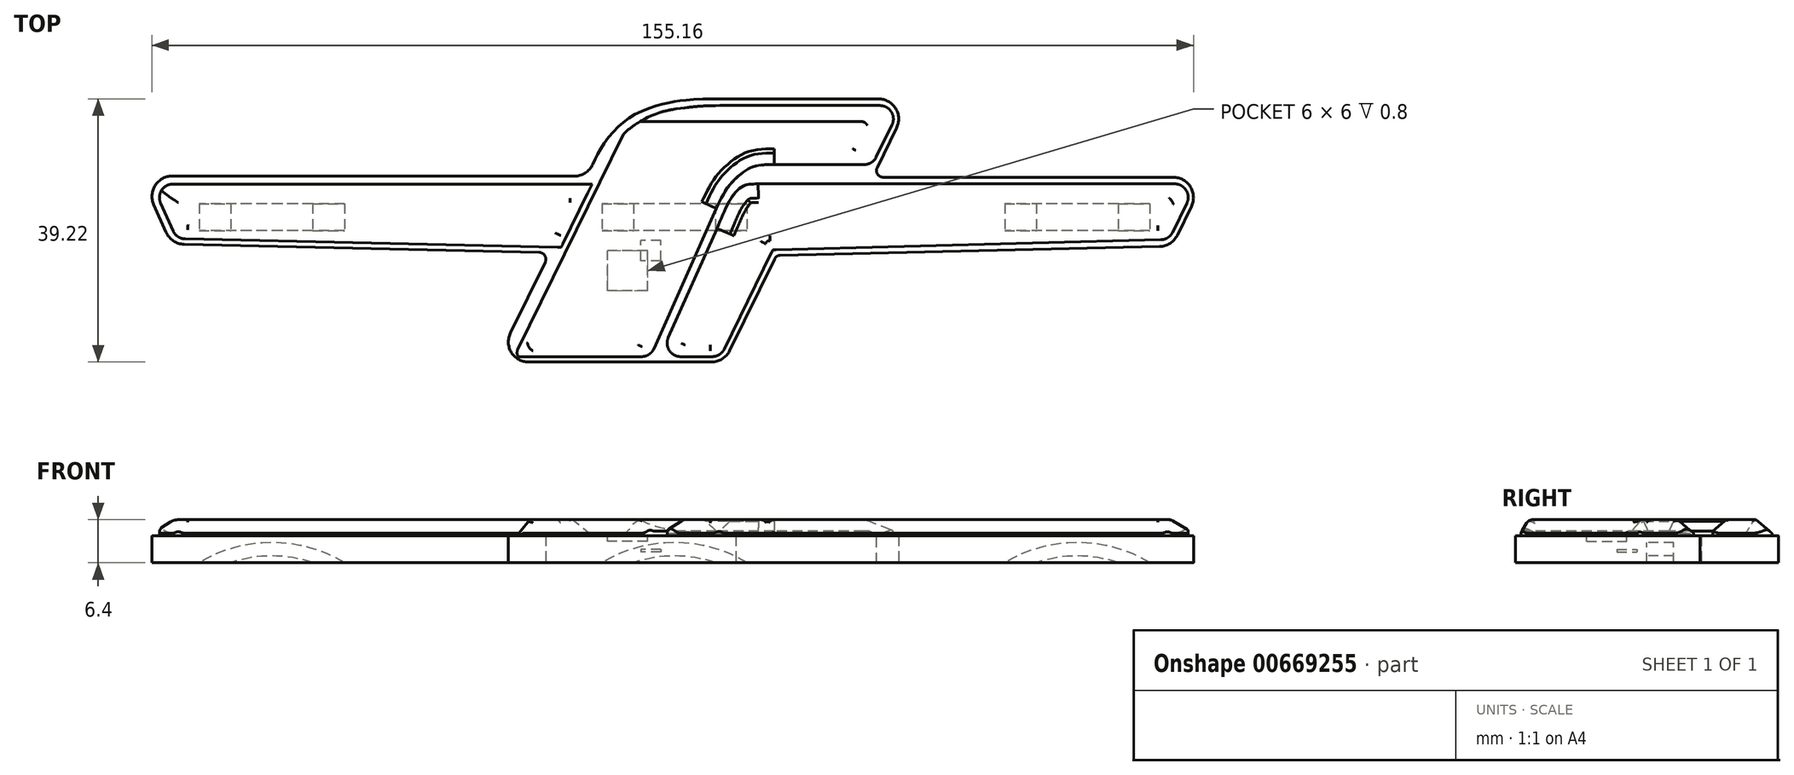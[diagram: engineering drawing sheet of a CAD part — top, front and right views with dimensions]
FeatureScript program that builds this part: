
annotation { "Feature Type Name" : "Feature", "Feature Type Description" : "" }
export const myFeature = defineFeature(function(context is Context, id is Id, definition is map)
    precondition{}
    {
        {
            var Q0;
            Q0=qCreatedBy(makeId("Top.planeOp"),FACE);
            var sketch = newSketch(context, id + "F0", { "sketchPlane" : qUnion([Q0])});
            skLineSegment(sketch, "E0", {"start": v(-9.3, -1.65) * mm, "end": v(-13.28, -9.8) * mm});
            skLineSegment(sketch, "E1", {"start": v(-13.28, -9.8) * mm, "end": v(3.7, -9.8) * mm});
            skLineSegment(sketch, "E2", {"start": v(3.7, -9.8) * mm, "end": v(7.58, -1.85) * mm});
            skLineSegment(sketch, "E3", {"start": v(-9.3, -1.65) * mm, "end": v(-37.48, -1) * mm});
            skLineSegment(sketch, "E4", {"start": v(-37.48, -1) * mm, "end": v(-39.73, 4.05) * mm});
            skLineSegment(sketch, "E5", {"start": v(-6.5, 4.05) * mm, "end": v(-39.73, 4.05) * mm});
            skLineSegment(sketch, "E6", {"start": v(7.58, -1.85) * mm, "end": v(37.05, -1.17) * mm});
            skLineSegment(sketch, "E7", {"start": v(37.05, -1.17) * mm, "end": v(39.56, 3.96) * mm});
            skLineSegment(sketch, "E8", {"start": v(39.56, 3.96) * mm, "end": v(14.75, 3.96) * mm});
            skLineSegment(sketch, "E9", {"start": v(14.75, 3.96) * mm, "end": v(17.6, 9.8) * mm});
            skLineSegment(sketch, "E10", {"start": v(17.6, 9.8) * mm, "end": v(4.58, 9.8) * mm});
            skLineSegment(sketch, "E11", {"start": v(-4.8, -9.8) * mm, "end": v(4.8, 9.8) * mm, "construction": true});
            skLineSegment(sketch, "E12", {"start": v(-9.3, -1.65) * mm, "end": v(-6.5, 4.05) * mm});
            skFitSpline(sketch, "E13", {"points": [v(-6.5, 4.05) * mm, v(-5.96, 5.22) * mm, v(-5.41, 6.24) * mm, v(-4.34, 7.56) * mm, v(-3.15, 8.53) * mm, v(-1.39, 9.28) * mm, v(-0.1, 9.58) * mm, v(1.1, 9.73) * mm, v(4.58, 9.8) * mm], "startDerivative": vector(5.08, 10.85) * mm, "endDerivative": vector(21.51, -0.42) * mm});
            skSolve(sketch);
        }
        {
            var Q0;
            Q0 = qSketchRegion(id + "F0", true);
            extrude(context, id + "F1", {"entities" : qUnion([Q0]), "depth" : 2 * mm, "offsetDistance" : 25 * mm});
        }
        {
            var Q0;
            Q0=makeQuery(id+"F1.opExtrude","CAP_FACE",FACE,{"disambiguationData":[OSD([sQuery(id+"F0.wireOp",EDGE,"E0"),sQuery(id+"F0.wireOp",EDGE,"E1"),sQuery(id+"F0.wireOp",EDGE,"E2"),sQuery(id+"F0.wireOp",EDGE,"E3"),sQuery(id+"F0.wireOp",EDGE,"E4"),sQuery(id+"F0.wireOp",EDGE,"E5"),sQuery(id+"F0.wireOp",EDGE,"E6"),sQuery(id+"F0.wireOp",EDGE,"E7"),sQuery(id+"F0.wireOp",EDGE,"E8"),sQuery(id+"F0.wireOp",EDGE,"E9"),sQuery(id+"F0.wireOp",EDGE,"E10"),sQuery(id+"F0.wireOp",EDGE,"b49870b3-532a-455c-8938-6e246f278ffe")])],"isStart":false});
            var sketch = newSketch(context, id + "F2", { "sketchPlane" : qUnion([Q0])});
            skLineSegment(sketch, "E14.0", {"start": v(-12.42, -9.4) * mm, "end": v(-1.8, -9.4) * mm});
            skLineSegment(sketch, "E14.2", {"start": v(-5.32, 5.12) * mm, "end": v(-12.42, -9.4) * mm});
            skLineSegment(sketch, "E14.4", {"start": v(-37.1, -0.61) * mm, "end": v(-8.44, -1.26) * mm});
            skLineSegment(sketch, "E14.7", {"start": v(-6.14, 3.45) * mm, "end": v(-38.9, 3.45) * mm});
            skLineSegment(sketch, "E14.9", {"start": v(-38.9, 3.45) * mm, "end": v(-37.1, -0.61) * mm});
            skLineSegment(sketch, "E14.14", {"start": v(7.32, -1.46) * mm, "end": v(36.84, -0.67) * mm});
            skLineSegment(sketch, "E14.16", {"start": v(36.84, -0.67) * mm, "end": v(38.87, 3.47) * mm});
            skLineSegment(sketch, "E14.18", {"start": v(38.87, 3.47) * mm, "end": v(6.25, 3.47) * mm});
            skLineSegment(sketch, "E14.20", {"start": v(14.76, 4.91) * mm, "end": v(16.9, 9.3) * mm});
            skLineSegment(sketch, "E14.22", {"start": v(16.9, 9.3) * mm, "end": v(4.7, 9.3) * mm});
            skLineSegment(sketch, "E15", {"start": v(3.12, 1.64) * mm, "end": v(-1.8, -9.4) * mm});
            skLineSegment(sketch, "E16", {"start": v(14.76, 4.91) * mm, "end": v(7.44, 4.91) * mm});
            skLineSegment(sketch, "E17", {"start": v(-5.85, 4.04) * mm, "end": v(-5.32, 5.12) * mm});
            skFitSpline(sketch, "E18", {"points": [v(-5.85, 4.04) * mm, v(-4.97, 5.75) * mm, v(-3.99, 7.02) * mm, v(-2.6, 8.1) * mm, v(-0.84, 8.86) * mm, v(0.9, 9.16) * mm, v(2.28, 9.28) * mm, v(4.7, 9.3) * mm], "startDerivative": vector(5.74, 12.1) * mm, "endDerivative": vector(15.8, -0.05) * mm});
            skFitSpline(sketch, "E19", {"points": [v(3.12, 1.64) * mm, v(3.63, 2.68) * mm, v(4.24, 3.55) * mm, v(4.98, 4.23) * mm, v(5.54, 4.61) * mm, v(6.09, 4.81) * mm, v(6.58, 4.89) * mm, v(7.44, 4.91) * mm], "startDerivative": vector(2.92, 6.26) * mm, "endDerivative": vector(6.3, 0.08) * mm});
            skLineSegment(sketch, "E20", {"start": v(-1.1, -9.4) * mm, "end": v(3.16, 0.16) * mm});
            skFitSpline(sketch, "E21", {"points": [v(3.16, 0.16) * mm, v(3.58, 1.14) * mm, v(4, 2.02) * mm, v(4.38, 2.63) * mm, v(4.79, 3.1) * mm, v(5.17, 3.33) * mm, v(5.46, 3.42) * mm, v(5.77, 3.46) * mm, v(6.25, 3.47) * mm], "startDerivative": vector(2.45, 5.8) * mm, "endDerivative": vector(4.54, 0.1) * mm});
            skLineSegment(sketch, "E22.trimOffspring", {"start": v(-1.1, -9.4) * mm, "end": v(3.43, -9.4) * mm});
            skLineSegment(sketch, "E23", {"start": v(3.43, -9.4) * mm, "end": v(7.32, -1.46) * mm});
            skSolve(sketch);
        }
        {
            var Q0;
            Q0=makeQuery(id+"F2.imprint","IMPRINT",FACE,{"disambiguationData":[TD([[makeQuery(id+"F2.imprint","IMPRINT",EDGE,{"derivedFrom":sQuery(id+"F2.wireOp",EDGE,"E14.0")}),-1.0]])]});
            var sketch = newSketch(context, id + "F3", { "sketchPlane" : qUnion([Q0])});
            skLineSegment(sketch, "E24.bottom", {"start": v(-2, -4.5) * mm, "end": v(-5, -4.5) * mm});
            skLineSegment(sketch, "E24.top", {"start": v(-2, -1.5) * mm, "end": v(-5, -1.5) * mm});
            skLineSegment(sketch, "E24.left", {"start": v(-2, -4.5) * mm, "end": v(-2, -1.5) * mm});
            skLineSegment(sketch, "E24.right", {"start": v(-5, -4.5) * mm, "end": v(-5, -1.5) * mm});
            skPoint(sketch, "E24.middle", {"position": v(-3.5, -3) * mm});
            skSolve(sketch);
        }
        {
            var Q0;
            Q0=makeQuery(id+"F3.imprint","IMPRINT",FACE,{"disambiguationData":[TD([[makeQuery(id+"F3.imprint","IMPRINT",EDGE,{"derivedFrom":sQuery(id+"F3.wireOp",EDGE,"E24.bottom")}),-1.0]])]});
            extrude(context, id + "F4", {"entities" : qUnion([Q0]), "operationType" : NewBodyOperationType.REMOVE, "oppositeDirection" : true, "depth" : .4 * mm, "offsetDistance" : 25 * mm});
        }
        {
            var Q0;
            Q0=makeQuery(id+"F4.boolean.opBoolean","COPY",FACE,{"derivedFrom":makeQuery(id+"F4.opExtrude","CAP_FACE",FACE,{"disambiguationData":[OSD([sQuery(id+"F3.wireOp",EDGE,"E24.bottom"),sQuery(id+"F3.wireOp",EDGE,"E24.top"),sQuery(id+"F3.wireOp",EDGE,"E24.left"),sQuery(id+"F3.wireOp",EDGE,"E24.right")])],"isStart":false})});
            extrude(context, id + "F5", {"entities" : qUnion([Q0]), "depth" : .4 * mm, "offsetDistance" : 25 * mm});
        }
        {
            var Q0;
            Q0=makeQuery(id+"F2.imprint","IMPRINT",FACE,{"disambiguationData":[TD([[makeQuery(id+"F2.imprint","IMPRINT",EDGE,{"derivedFrom":sQuery(id+"F2.wireOp",EDGE,"E14.0")}),1.0]])]});
            var Q1;
            Q1=makeQuery(id+"F2.imprint","IMPRINT",FACE,{"disambiguationData":[TD([[makeQuery(id+"F2.imprint","IMPRINT",EDGE,{"derivedFrom":sQuery(id+"F2.wireOp",EDGE,"E14.12")}),1.0]])]});
            var Q2;
            Q2=makeQuery(id+"F2.imprint","IMPRINT",FACE,{"disambiguationData":[TD([[makeQuery(id+"F2.imprint","IMPRINT",EDGE,{"derivedFrom":sQuery(id+"F2.wireOp",EDGE,"E14.14")}),1.0]])]});
            extrude(context, id + "F6", {"entities" : qUnion([Q0, Q1, Q2]), "depth" : 1.2 * mm, "offsetDistance" : 25 * mm});
        }
        {
            var Q0;
            {var subQ1=sQuery(id+"F2.wireOp",EDGE,"E14.4");Q0=makeQuery(id+"F2.imprint","IMPRINT",FACE,{"disambiguationData":[TD([[makeQuery(id+"F2.imprint","IMPRINT",EDGE,{"derivedFrom":subQ1}),1.0]])]});}
            extrude(context, id + "F7", {"entities" : qUnion([Q0]), "depth" : 1.2 * mm, "offsetDistance" : 25 * mm});
        }
        {
            var Q0;
            Q0=makeQuery(id+"F7.opExtrude","CAP_EDGE",EDGE,{"disambiguationData":[OSD([sQuery(id+"F2.wireOp",EDGE,"E14.7")])],"isStart":false});
            var Q1;
            Q1=makeQuery(id+"F6.opExtrude","CAP_EDGE",EDGE,{"disambiguationData":[OSD([sQuery(id+"F2.wireOp",EDGE,"E14.18")])],"isStart":false});
            chamfer(context, id + "F8", {"entities" : qUnion([Q0, Q1]), "chamferType" : ChamferType.OFFSET_ANGLE, "width" : 1 * mm, "oppositeDirection" : true, "angle" : 50 * degree, "tangentPropagation" : true});
        }
        {
            var Q0;
            Q0=makeQuery(id+"F6.opExtrude","CAP_EDGE",EDGE,{"disambiguationData":[OSD([sQuery(id+"F2.wireOp",EDGE,"E14.14")])],"isStart":false});
            var Q1;
            Q1=makeQuery(id+"F7.opExtrude","CAP_EDGE",EDGE,{"disambiguationData":[OSD([sQuery(id+"F2.wireOp",EDGE,"E14.4")])],"isStart":false});
            var Q2;
            Q2=makeQuery(id+"F6.opExtrude","CAP_EDGE",EDGE,{"disambiguationData":[OSD([sQuery(id+"F2.wireOp",EDGE,"E15")])],"isStart":false});
            var Q3;
            Q3=makeQuery(id+"F6.opExtrude","CAP_EDGE",EDGE,{"disambiguationData":[OSD([sQuery(id+"F2.wireOp",EDGE,"E16")])],"isStart":false});
            var Q4;
            Q4=makeQuery(id+"F6.opExtrude","CAP_EDGE",EDGE,{"disambiguationData":[OSD([sQuery(id+"F2.wireOp",EDGE,"E19")])],"isStart":false});
            var Q5;
            Q5=makeQuery(id+"F6.opExtrude","CAP_EDGE",EDGE,{"disambiguationData":[OSD([sQuery(id+"F2.wireOp",EDGE,"E23")])],"isStart":false});
            chamfer(context, id + "F9", {"entities" : qUnion([Q0, Q1, Q2, Q3, Q4, Q5]), "chamferType" : ChamferType.OFFSET_ANGLE, "width" : 1 * mm, "oppositeDirection" : true, "angle" : 40 * degree, "tangentPropagation" : true});
        }
        {
            var Q0;
            Q0=makeQuery(id+"F6.opExtrude","CAP_EDGE",EDGE,{"disambiguationData":[OSD([sQuery(id+"F2.wireOp",EDGE,"E14.2"),sQuery(id+"F2.wireOp",EDGE,"E17")])],"isStart":false});
            chamfer(context, id + "F10", {"entities" : qUnion([Q0]), "chamferType" : ChamferType.OFFSET_ANGLE, "width" : 1 * mm, "oppositeDirection" : false, "angle" : 65 * degree});
        }
        {
            var Q0;
            Q0=makeQuery(id+"F6.opExtrude","CAP_EDGE",EDGE,{"disambiguationData":[OSD([sQuery(id+"F2.wireOp",EDGE,"E14.22")])],"isStart":false});
            chamfer(context, id + "F11", {"entities" : qUnion([Q0]), "chamferType" : ChamferType.OFFSET_ANGLE, "width" : 1 * mm, "oppositeDirection" : true, "angle" : 50 * degree, "tangentPropagation" : true});
        }
        {
            var Q0;
            Q0=makeQuery(id+"F6.opExtrude","CAP_EDGE",EDGE,{"disambiguationData":[OSD([sQuery(id+"F2.wireOp",EDGE,"E14.20")])],"isStart":false});
            chamfer(context, id + "F12", {"entities" : qUnion([Q0]), "chamferType" : ChamferType.OFFSET_ANGLE, "width" : 1 * mm, "oppositeDirection" : true, "angle" : 60 * degree, "tangentPropagation" : true});
        }
        {
            var Q0;
            Q0=makeQuery(id+"F6.opExtrude","CAP_EDGE",EDGE,{"disambiguationData":[OSD([sQuery(id+"F2.wireOp",EDGE,"E14.0")])],"isStart":false});
            var Q1;
            Q1=makeQuery(id+"F6.opExtrude","CAP_EDGE",EDGE,{"disambiguationData":[OSD([sQuery(id+"F2.wireOp",EDGE,"E22.trimOffspring")])],"isStart":false});
            chamfer(context, id + "F13", {"entities" : qUnion([Q0, Q1]), "chamferType" : ChamferType.OFFSET_ANGLE, "width" : 1 * mm, "oppositeDirection" : true, "angle" : 30 * degree, "tangentPropagation" : true});
        }
        {
            var Q0;
            Q0=makeQuery(id+"F7.opExtrude","CAP_EDGE",EDGE,{"disambiguationData":[OSD([sQuery(id+"F2.wireOp",EDGE,"E14.2")])],"isStart":false});
            chamfer(context, id + "F14", {"entities" : qUnion([Q0]), "chamferType" : ChamferType.OFFSET_ANGLE, "width" : 1 * mm, "oppositeDirection" : false, "angle" : 30 * degree, "tangentPropagation" : true});
        }
        {
            var Q0;
            Q0=makeQuery(id+"F7.opExtrude","CAP_EDGE",EDGE,{"disambiguationData":[OSD([sQuery(id+"F2.wireOp",EDGE,"E14.9")])],"isStart":false});
            var Q1;
            Q1=makeQuery(id+"F6.opExtrude","CAP_EDGE",EDGE,{"disambiguationData":[OSD([sQuery(id+"F2.wireOp",EDGE,"E14.16")])],"isStart":false});
            chamfer(context, id + "F15", {"entities" : qUnion([Q0, Q1]), "chamferType" : ChamferType.OFFSET_ANGLE, "width" : 1 * mm, "oppositeDirection" : false, "angle" : 45 * degree, "tangentPropagation" : true});
        }
        {
            var Q0;
            Q0=makeQuery(id+"F6.opExtrude","CAP_EDGE",EDGE,{"disambiguationData":[OSD([sQuery(id+"F2.wireOp",EDGE,"E20")])],"isStart":false});
            var Q1;
            Q1=makeQuery(id+"F6.opExtrude","CAP_EDGE",EDGE,{"disambiguationData":[OSD([sQuery(id+"F2.wireOp",EDGE,"E21")])],"isStart":false});
            chamfer(context, id + "F16", {"entities" : qUnion([Q0, Q1]), "chamferType" : ChamferType.OFFSET_ANGLE, "width" : 1 * mm, "oppositeDirection" : false, "angle" : 50 * degree, "tangentPropagation" : true});
        }
        {
            var Q0;
            Q0=makeQuery(id+"F1.opExtrude","SWEPT_EDGE",EDGE,{"disambiguationData":[OSD([sQuery(id+"F0.wireOp",EDGE,"E2"),sQuery(id+"F0.wireOp",EDGE,"E6")])]});
            var Q1;
            Q1=makeQuery(id+"F1.opExtrude","SWEPT_EDGE",EDGE,{"disambiguationData":[OSD([sQuery(id+"F0.wireOp",EDGE,"E8"),sQuery(id+"F0.wireOp",EDGE,"E9")])]});
            var Q2;
            Q2=makeQuery(id+"F1.opExtrude","SWEPT_EDGE",EDGE,{"disambiguationData":[OSD([sQuery(id+"F0.wireOp",EDGE,"E0"),sQuery(id+"F0.wireOp",EDGE,"E3"),sQuery(id+"F0.wireOp",EDGE,"E12")])]});
            fillet(context, id + "F17", {"entities" : qUnion([Q0, Q1, Q2]), "radius" : .5 * mm, "tangentPropagation" : true, "allowEdgeOverflow" : false});
        }
        {
            var Q0;
            Q0=makeQuery(id+"F11.opChamfer","BLEND_EDGE",EDGE,{"blendedFrom":[makeQuery(id+"F6.opExtrude","CAP_EDGE",EDGE,{"disambiguationData":[OSD([sQuery(id+"F2.wireOp",EDGE,"E18")])],"isStart":false}),makeQuery(id+"F10.opChamfer","BLEND_FACE",FACE,{"disambiguationData":[OSD([sQuery(id+"F2.wireOp",EDGE,"E14.2"),sQuery(id+"F2.wireOp",EDGE,"E17")])]})],"blendedInto":[makeQuery(id+"F10.opChamfer","BLEND_FACE",FACE,{"disambiguationData":[OSD([sQuery(id+"F2.wireOp",EDGE,"E14.2"),sQuery(id+"F2.wireOp",EDGE,"E17")])]})]});
            var Q1;
            Q1=makeQuery(id+"F16.opChamfer","BLEND_EDGE",EDGE,{"blendedFrom":[makeQuery(id+"F6.opExtrude","CAP_EDGE",EDGE,{"disambiguationData":[OSD([sQuery(id+"F2.wireOp",EDGE,"E21")])],"isStart":false}),makeQuery(id+"F8.opChamfer","BLEND_FACE",FACE,{"disambiguationData":[OSD([sQuery(id+"F2.wireOp",EDGE,"E14.18")])]})],"blendedInto":[makeQuery(id+"F8.opChamfer","BLEND_FACE",FACE,{"disambiguationData":[OSD([sQuery(id+"F2.wireOp",EDGE,"E14.18")])]})]});
            fillet(context, id + "F18", {"entities" : qUnion([Q0, Q1]), "radius" : 2 * mm, "tangentPropagation" : true, "allowEdgeOverflow" : false});
        }
        {
            var Q0;
            Q0=makeQuery(id+"F7.opExtrude","SWEPT_EDGE",EDGE,{"disambiguationData":[OSD([sQuery(id+"F2.wireOp",EDGE,"E14.4"),sQuery(id+"F2.wireOp",EDGE,"E14.9")])]});
            var Q1;
            Q1=makeQuery(id+"F7.opExtrude","SWEPT_EDGE",EDGE,{"disambiguationData":[OSD([sQuery(id+"F2.wireOp",EDGE,"E14.7"),sQuery(id+"F2.wireOp",EDGE,"E14.9")])]});
            var Q2;
            Q2=makeQuery(id+"F6.opExtrude","SWEPT_EDGE",EDGE,{"disambiguationData":[OSD([sQuery(id+"F2.wireOp",EDGE,"E14.0"),sQuery(id+"F2.wireOp",EDGE,"E14.2")])]});
            var Q3;
            Q3=makeQuery(id+"F6.opExtrude","SWEPT_EDGE",EDGE,{"disambiguationData":[OSD([sQuery(id+"F2.wireOp",EDGE,"E22.trimOffspring"),sQuery(id+"F2.wireOp",EDGE,"E23")])]});
            var Q4;
            Q4=makeQuery(id+"F6.opExtrude","SWEPT_EDGE",EDGE,{"disambiguationData":[OSD([sQuery(id+"F2.wireOp",EDGE,"E20"),sQuery(id+"F2.wireOp",EDGE,"E22.trimOffspring")])]});
            var Q5;
            Q5=makeQuery(id+"F6.opExtrude","SWEPT_EDGE",EDGE,{"disambiguationData":[OSD([sQuery(id+"F2.wireOp",EDGE,"E14.14"),sQuery(id+"F2.wireOp",EDGE,"E14.16")])]});
            var Q6;
            Q6=makeQuery(id+"F6.opExtrude","SWEPT_EDGE",EDGE,{"disambiguationData":[OSD([sQuery(id+"F2.wireOp",EDGE,"E14.16"),sQuery(id+"F2.wireOp",EDGE,"E14.18")])]});
            var Q7;
            Q7=makeQuery(id+"F6.opExtrude","SWEPT_EDGE",EDGE,{"disambiguationData":[OSD([sQuery(id+"F2.wireOp",EDGE,"E14.20"),sQuery(id+"F2.wireOp",EDGE,"E16")])]});
            var Q8;
            Q8=makeQuery(id+"F6.opExtrude","SWEPT_EDGE",EDGE,{"disambiguationData":[OSD([sQuery(id+"F2.wireOp",EDGE,"E14.20"),sQuery(id+"F2.wireOp",EDGE,"E14.22")])]});
            var Q9;
            Q9=makeQuery(id+"F6.opExtrude","SWEPT_EDGE",EDGE,{"disambiguationData":[OSD([sQuery(id+"F2.wireOp",EDGE,"E14.0"),sQuery(id+"F2.wireOp",EDGE,"E15")])]});
            fillet(context, id + "F19", {"entities" : qUnion([Q0, Q1, Q2, Q3, Q4, Q5, Q6, Q7, Q8, Q9]), "radius" : 1 * mm, "tangentPropagation" : true, "allowEdgeOverflow" : false});
        }
        {
            var Q0;
            Q0=makeQuery(id+"F1.opExtrude","SWEPT_EDGE",EDGE,{"disambiguationData":[OSD([sQuery(id+"F0.wireOp",EDGE,"E0"),sQuery(id+"F0.wireOp",EDGE,"E1")])]});
            var Q1;
            Q1=makeQuery(id+"F1.opExtrude","SWEPT_EDGE",EDGE,{"disambiguationData":[OSD([sQuery(id+"F0.wireOp",EDGE,"E3"),sQuery(id+"F0.wireOp",EDGE,"E4")])]});
            var Q2;
            Q2=makeQuery(id+"F1.opExtrude","SWEPT_EDGE",EDGE,{"disambiguationData":[OSD([sQuery(id+"F0.wireOp",EDGE,"E4"),sQuery(id+"F0.wireOp",EDGE,"E5")])]});
            var Q3;
            Q3=makeQuery(id+"F1.opExtrude","SWEPT_EDGE",EDGE,{"disambiguationData":[OSD([sQuery(id+"F0.wireOp",EDGE,"E5"),sQuery(id+"F0.wireOp",EDGE,"E12"),sQuery(id+"F0.wireOp",EDGE,"E13")])]});
            var Q4;
            Q4=makeQuery(id+"F1.opExtrude","SWEPT_EDGE",EDGE,{"disambiguationData":[OSD([sQuery(id+"F0.wireOp",EDGE,"E9"),sQuery(id+"F0.wireOp",EDGE,"E10")])]});
            var Q5;
            Q5=makeQuery(id+"F1.opExtrude","SWEPT_EDGE",EDGE,{"disambiguationData":[OSD([sQuery(id+"F0.wireOp",EDGE,"E7"),sQuery(id+"F0.wireOp",EDGE,"E8")])]});
            var Q6;
            Q6=makeQuery(id+"F1.opExtrude","SWEPT_EDGE",EDGE,{"disambiguationData":[OSD([sQuery(id+"F0.wireOp",EDGE,"E6"),sQuery(id+"F0.wireOp",EDGE,"E7")])]});
            var Q7;
            Q7=makeQuery(id+"F1.opExtrude","SWEPT_EDGE",EDGE,{"disambiguationData":[OSD([sQuery(id+"F0.wireOp",EDGE,"E1"),sQuery(id+"F0.wireOp",EDGE,"E2")])]});
            fillet(context, id + "F20", {"entities" : qUnion([Q0, Q1, Q2, Q3, Q4, Q5, Q6, Q7]), "radius" : 1.5 * mm, "tangentPropagation" : true, "allowEdgeOverflow" : false});
        }
        {
            var Q0;
            {var subQ0=sQuery(id+"F2.wireOp",EDGE,"E14.4");Q0=makeQuery(id+"F9.opChamfer","BLEND_EDGE",EDGE,{"blendedFrom":[makeQuery(id+"F7.opExtrude","CAP_EDGE",EDGE,{"disambiguationData":[OSD([subQ0])],"isStart":false}),makeQuery(id+"F7.opExtrude","CAP_FACE",FACE,{"disambiguationData":[OSD([sQuery(id+"F2.wireOp",EDGE,"E14.2"),subQ0,sQuery(id+"F2.wireOp",EDGE,"E14.7"),sQuery(id+"F2.wireOp",EDGE,"E14.9")])],"isStart":false})],"blendedInto":[makeQuery(id+"F7.opExtrude","CAP_FACE",FACE,{"disambiguationData":[OSD([sQuery(id+"F2.wireOp",EDGE,"E14.2"),subQ0,sQuery(id+"F2.wireOp",EDGE,"E14.7"),sQuery(id+"F2.wireOp",EDGE,"E14.9")])],"isStart":false})]});}
            var Q1;
            Q1=makeQuery(id+"F15.opChamfer","BLEND_EDGE",EDGE,{"blendedFrom":[makeQuery(id+"F7.opExtrude","CAP_EDGE",EDGE,{"disambiguationData":[OSD([sQuery(id+"F2.wireOp",EDGE,"E14.9")])],"isStart":false}),makeQuery(id+"F9.opChamfer","BLEND_FACE",FACE,{"disambiguationData":[OSD([sQuery(id+"F2.wireOp",EDGE,"E14.4")])]})],"blendedInto":[makeQuery(id+"F9.opChamfer","BLEND_FACE",FACE,{"disambiguationData":[OSD([sQuery(id+"F2.wireOp",EDGE,"E14.4")])]})]});
            var Q2;
            {var subQ0=sQuery(id+"F2.wireOp",EDGE,"E14.9");Q2=makeQuery(id+"F15.opChamfer","BLEND_EDGE",EDGE,{"blendedFrom":[makeQuery(id+"F7.opExtrude","CAP_EDGE",EDGE,{"disambiguationData":[OSD([subQ0])],"isStart":false}),makeQuery(id+"F7.opExtrude","CAP_FACE",FACE,{"disambiguationData":[OSD([sQuery(id+"F2.wireOp",EDGE,"E14.2"),sQuery(id+"F2.wireOp",EDGE,"E14.4"),sQuery(id+"F2.wireOp",EDGE,"E14.7"),subQ0])],"isStart":false})],"blendedInto":[makeQuery(id+"F7.opExtrude","CAP_FACE",FACE,{"disambiguationData":[OSD([sQuery(id+"F2.wireOp",EDGE,"E14.2"),sQuery(id+"F2.wireOp",EDGE,"E14.4"),sQuery(id+"F2.wireOp",EDGE,"E14.7"),subQ0])],"isStart":false})]});}
            var Q3;
            {var subQ0=sQuery(id+"F2.wireOp",EDGE,"E14.7");Q3=makeQuery(id+"F8.opChamfer","BLEND_EDGE",EDGE,{"blendedFrom":[makeQuery(id+"F7.opExtrude","CAP_EDGE",EDGE,{"disambiguationData":[OSD([subQ0])],"isStart":false}),makeQuery(id+"F7.opExtrude","CAP_FACE",FACE,{"disambiguationData":[OSD([sQuery(id+"F2.wireOp",EDGE,"E14.2"),sQuery(id+"F2.wireOp",EDGE,"E14.4"),subQ0,sQuery(id+"F2.wireOp",EDGE,"E14.9")])],"isStart":false})],"blendedInto":[makeQuery(id+"F7.opExtrude","CAP_FACE",FACE,{"disambiguationData":[OSD([sQuery(id+"F2.wireOp",EDGE,"E14.2"),sQuery(id+"F2.wireOp",EDGE,"E14.4"),subQ0,sQuery(id+"F2.wireOp",EDGE,"E14.9")])],"isStart":false})]});}
            var Q4;
            {var subQ0=sQuery(id+"F2.wireOp",EDGE,"E14.2");Q4=makeQuery(id+"F14.opChamfer","BLEND_EDGE",EDGE,{"blendedFrom":[makeQuery(id+"F7.opExtrude","CAP_EDGE",EDGE,{"disambiguationData":[OSD([subQ0])],"isStart":false}),makeQuery(id+"F7.opExtrude","CAP_FACE",FACE,{"disambiguationData":[OSD([subQ0,sQuery(id+"F2.wireOp",EDGE,"E14.4"),sQuery(id+"F2.wireOp",EDGE,"E14.7"),sQuery(id+"F2.wireOp",EDGE,"E14.9")])],"isStart":false})],"blendedInto":[makeQuery(id+"F7.opExtrude","CAP_FACE",FACE,{"disambiguationData":[OSD([subQ0,sQuery(id+"F2.wireOp",EDGE,"E14.4"),sQuery(id+"F2.wireOp",EDGE,"E14.7"),sQuery(id+"F2.wireOp",EDGE,"E14.9")])],"isStart":false})]});}
            var Q5;
            Q5=makeQuery(id+"F14.opChamfer","BLEND_EDGE",EDGE,{"blendedFrom":[makeQuery(id+"F7.opExtrude","CAP_EDGE",EDGE,{"disambiguationData":[OSD([sQuery(id+"F2.wireOp",EDGE,"E14.2")])],"isStart":false}),makeQuery(id+"F9.opChamfer","BLEND_FACE",FACE,{"disambiguationData":[OSD([sQuery(id+"F2.wireOp",EDGE,"E14.4")])]})],"blendedInto":[makeQuery(id+"F9.opChamfer","BLEND_FACE",FACE,{"disambiguationData":[OSD([sQuery(id+"F2.wireOp",EDGE,"E14.4")])]})]});
            var Q6;
            Q6=makeQuery(id+"F14.opChamfer","BLEND_EDGE",EDGE,{"blendedFrom":[makeQuery(id+"F7.opExtrude","CAP_EDGE",EDGE,{"disambiguationData":[OSD([sQuery(id+"F2.wireOp",EDGE,"E14.2")])],"isStart":false}),makeQuery(id+"F8.opChamfer","BLEND_FACE",FACE,{"disambiguationData":[OSD([sQuery(id+"F2.wireOp",EDGE,"E14.7")])]})],"blendedInto":[makeQuery(id+"F8.opChamfer","BLEND_FACE",FACE,{"disambiguationData":[OSD([sQuery(id+"F2.wireOp",EDGE,"E14.7")])]})]});
            var Q7;
            {var subQ0=sQuery(id+"F2.wireOp",EDGE,"E17");var subQ1=sQuery(id+"F2.wireOp",EDGE,"E14.2");Q7=makeQuery(id+"F10.opChamfer","BLEND_EDGE",EDGE,{"blendedFrom":[makeQuery(id+"F6.opExtrude","CAP_EDGE",EDGE,{"disambiguationData":[OSD([subQ1,subQ0])],"isStart":false}),makeQuery(id+"F6.opExtrude","CAP_FACE",FACE,{"disambiguationData":[OSD([sQuery(id+"F2.wireOp",EDGE,"E14.0"),subQ1,sQuery(id+"F2.wireOp",EDGE,"E14.20"),sQuery(id+"F2.wireOp",EDGE,"E14.22"),sQuery(id+"F2.wireOp",EDGE,"E15"),sQuery(id+"F2.wireOp",EDGE,"E16"),subQ0,sQuery(id+"F2.wireOp",EDGE,"E18"),sQuery(id+"F2.wireOp",EDGE,"E19")])],"isStart":false})],"blendedInto":[makeQuery(id+"F6.opExtrude","CAP_FACE",FACE,{"disambiguationData":[OSD([sQuery(id+"F2.wireOp",EDGE,"E14.0"),subQ1,sQuery(id+"F2.wireOp",EDGE,"E14.20"),sQuery(id+"F2.wireOp",EDGE,"E14.22"),sQuery(id+"F2.wireOp",EDGE,"E15"),sQuery(id+"F2.wireOp",EDGE,"E16"),subQ0,sQuery(id+"F2.wireOp",EDGE,"E18"),sQuery(id+"F2.wireOp",EDGE,"E19")])],"isStart":false})]});}
            var Q8;
            {var subQ0=sQuery(id+"F2.wireOp",EDGE,"E14.0");Q8=makeQuery(id+"F13.opChamfer","BLEND_EDGE",EDGE,{"blendedFrom":[makeQuery(id+"F6.opExtrude","CAP_EDGE",EDGE,{"disambiguationData":[OSD([subQ0])],"isStart":false}),makeQuery(id+"F6.opExtrude","CAP_FACE",FACE,{"disambiguationData":[OSD([subQ0,sQuery(id+"F2.wireOp",EDGE,"E14.2"),sQuery(id+"F2.wireOp",EDGE,"E14.20"),sQuery(id+"F2.wireOp",EDGE,"E14.22"),sQuery(id+"F2.wireOp",EDGE,"E15"),sQuery(id+"F2.wireOp",EDGE,"E16"),sQuery(id+"F2.wireOp",EDGE,"E17"),sQuery(id+"F2.wireOp",EDGE,"E18"),sQuery(id+"F2.wireOp",EDGE,"E19")])],"isStart":false})],"blendedInto":[makeQuery(id+"F6.opExtrude","CAP_FACE",FACE,{"disambiguationData":[OSD([subQ0,sQuery(id+"F2.wireOp",EDGE,"E14.2"),sQuery(id+"F2.wireOp",EDGE,"E14.20"),sQuery(id+"F2.wireOp",EDGE,"E14.22"),sQuery(id+"F2.wireOp",EDGE,"E15"),sQuery(id+"F2.wireOp",EDGE,"E16"),sQuery(id+"F2.wireOp",EDGE,"E17"),sQuery(id+"F2.wireOp",EDGE,"E18"),sQuery(id+"F2.wireOp",EDGE,"E19")])],"isStart":false})]});}
            var Q9;
            Q9=makeQuery(id+"F13.opChamfer","BLEND_EDGE",EDGE,{"blendedFrom":[makeQuery(id+"F6.opExtrude","CAP_EDGE",EDGE,{"disambiguationData":[OSD([sQuery(id+"F2.wireOp",EDGE,"E14.0")])],"isStart":false}),makeQuery(id+"F10.opChamfer","BLEND_FACE",FACE,{"disambiguationData":[OSD([sQuery(id+"F2.wireOp",EDGE,"E14.2"),sQuery(id+"F2.wireOp",EDGE,"E17")])]})],"blendedInto":[makeQuery(id+"F10.opChamfer","BLEND_FACE",FACE,{"disambiguationData":[OSD([sQuery(id+"F2.wireOp",EDGE,"E14.2"),sQuery(id+"F2.wireOp",EDGE,"E17")])]})]});
            var Q10;
            Q10=makeQuery(id+"F13.opChamfer","BLEND_EDGE",EDGE,{"blendedFrom":[makeQuery(id+"F6.opExtrude","CAP_EDGE",EDGE,{"disambiguationData":[OSD([sQuery(id+"F2.wireOp",EDGE,"E14.0")])],"isStart":false}),makeQuery(id+"F9.opChamfer","BLEND_FACE",FACE,{"disambiguationData":[OSD([sQuery(id+"F2.wireOp",EDGE,"E15")])]})],"blendedInto":[makeQuery(id+"F9.opChamfer","BLEND_FACE",FACE,{"disambiguationData":[OSD([sQuery(id+"F2.wireOp",EDGE,"E15")])]})]});
            var Q11;
            {var subQ0=sQuery(id+"F2.wireOp",EDGE,"E15");Q11=makeQuery(id+"F9.opChamfer","BLEND_EDGE",EDGE,{"blendedFrom":[makeQuery(id+"F6.opExtrude","CAP_EDGE",EDGE,{"disambiguationData":[OSD([subQ0])],"isStart":false}),makeQuery(id+"F6.opExtrude","CAP_FACE",FACE,{"disambiguationData":[OSD([sQuery(id+"F2.wireOp",EDGE,"E14.0"),sQuery(id+"F2.wireOp",EDGE,"E14.2"),sQuery(id+"F2.wireOp",EDGE,"E14.20"),sQuery(id+"F2.wireOp",EDGE,"E14.22"),subQ0,sQuery(id+"F2.wireOp",EDGE,"E16"),sQuery(id+"F2.wireOp",EDGE,"E17"),sQuery(id+"F2.wireOp",EDGE,"E18"),sQuery(id+"F2.wireOp",EDGE,"E19")])],"isStart":false})],"blendedInto":[makeQuery(id+"F6.opExtrude","CAP_FACE",FACE,{"disambiguationData":[OSD([sQuery(id+"F2.wireOp",EDGE,"E14.0"),sQuery(id+"F2.wireOp",EDGE,"E14.2"),sQuery(id+"F2.wireOp",EDGE,"E14.20"),sQuery(id+"F2.wireOp",EDGE,"E14.22"),subQ0,sQuery(id+"F2.wireOp",EDGE,"E16"),sQuery(id+"F2.wireOp",EDGE,"E17"),sQuery(id+"F2.wireOp",EDGE,"E18"),sQuery(id+"F2.wireOp",EDGE,"E19")])],"isStart":false})]});}
            var Q12;
            {var subQ0=sQuery(id+"F2.wireOp",EDGE,"E19");Q12=makeQuery(id+"F9.opChamfer","BLEND_EDGE",EDGE,{"blendedFrom":[makeQuery(id+"F6.opExtrude","CAP_EDGE",EDGE,{"disambiguationData":[OSD([subQ0])],"isStart":false}),makeQuery(id+"F6.opExtrude","CAP_FACE",FACE,{"disambiguationData":[OSD([sQuery(id+"F2.wireOp",EDGE,"E14.0"),sQuery(id+"F2.wireOp",EDGE,"E14.2"),sQuery(id+"F2.wireOp",EDGE,"E14.20"),sQuery(id+"F2.wireOp",EDGE,"E14.22"),sQuery(id+"F2.wireOp",EDGE,"E15"),sQuery(id+"F2.wireOp",EDGE,"E16"),sQuery(id+"F2.wireOp",EDGE,"E17"),sQuery(id+"F2.wireOp",EDGE,"E18"),subQ0])],"isStart":false})],"blendedInto":[makeQuery(id+"F6.opExtrude","CAP_FACE",FACE,{"disambiguationData":[OSD([sQuery(id+"F2.wireOp",EDGE,"E14.0"),sQuery(id+"F2.wireOp",EDGE,"E14.2"),sQuery(id+"F2.wireOp",EDGE,"E14.20"),sQuery(id+"F2.wireOp",EDGE,"E14.22"),sQuery(id+"F2.wireOp",EDGE,"E15"),sQuery(id+"F2.wireOp",EDGE,"E16"),sQuery(id+"F2.wireOp",EDGE,"E17"),sQuery(id+"F2.wireOp",EDGE,"E18"),subQ0])],"isStart":false})]});}
            var Q13;
            {var subQ0=sQuery(id+"F2.wireOp",EDGE,"E16");Q13=makeQuery(id+"F9.opChamfer","BLEND_EDGE",EDGE,{"blendedFrom":[makeQuery(id+"F6.opExtrude","CAP_EDGE",EDGE,{"disambiguationData":[OSD([subQ0])],"isStart":false}),makeQuery(id+"F6.opExtrude","CAP_FACE",FACE,{"disambiguationData":[OSD([sQuery(id+"F2.wireOp",EDGE,"E14.0"),sQuery(id+"F2.wireOp",EDGE,"E14.2"),sQuery(id+"F2.wireOp",EDGE,"E14.20"),sQuery(id+"F2.wireOp",EDGE,"E14.22"),sQuery(id+"F2.wireOp",EDGE,"E15"),subQ0,sQuery(id+"F2.wireOp",EDGE,"E17"),sQuery(id+"F2.wireOp",EDGE,"E18"),sQuery(id+"F2.wireOp",EDGE,"E19")])],"isStart":false})],"blendedInto":[makeQuery(id+"F6.opExtrude","CAP_FACE",FACE,{"disambiguationData":[OSD([sQuery(id+"F2.wireOp",EDGE,"E14.0"),sQuery(id+"F2.wireOp",EDGE,"E14.2"),sQuery(id+"F2.wireOp",EDGE,"E14.20"),sQuery(id+"F2.wireOp",EDGE,"E14.22"),sQuery(id+"F2.wireOp",EDGE,"E15"),subQ0,sQuery(id+"F2.wireOp",EDGE,"E17"),sQuery(id+"F2.wireOp",EDGE,"E18"),sQuery(id+"F2.wireOp",EDGE,"E19")])],"isStart":false})]});}
            var Q14;
            {var subQ0=sQuery(id+"F2.wireOp",EDGE,"E14.20");Q14=makeQuery(id+"F12.opChamfer","BLEND_EDGE",EDGE,{"blendedFrom":[makeQuery(id+"F6.opExtrude","CAP_EDGE",EDGE,{"disambiguationData":[OSD([subQ0])],"isStart":false}),makeQuery(id+"F6.opExtrude","CAP_FACE",FACE,{"disambiguationData":[OSD([sQuery(id+"F2.wireOp",EDGE,"E14.0"),sQuery(id+"F2.wireOp",EDGE,"E14.2"),subQ0,sQuery(id+"F2.wireOp",EDGE,"E14.22"),sQuery(id+"F2.wireOp",EDGE,"E15"),sQuery(id+"F2.wireOp",EDGE,"E16"),sQuery(id+"F2.wireOp",EDGE,"E17"),sQuery(id+"F2.wireOp",EDGE,"E18"),sQuery(id+"F2.wireOp",EDGE,"E19")])],"isStart":false})],"blendedInto":[makeQuery(id+"F6.opExtrude","CAP_FACE",FACE,{"disambiguationData":[OSD([sQuery(id+"F2.wireOp",EDGE,"E14.0"),sQuery(id+"F2.wireOp",EDGE,"E14.2"),subQ0,sQuery(id+"F2.wireOp",EDGE,"E14.22"),sQuery(id+"F2.wireOp",EDGE,"E15"),sQuery(id+"F2.wireOp",EDGE,"E16"),sQuery(id+"F2.wireOp",EDGE,"E17"),sQuery(id+"F2.wireOp",EDGE,"E18"),sQuery(id+"F2.wireOp",EDGE,"E19")])],"isStart":false})]});}
            var Q15;
            Q15=makeQuery(id+"F6.opExtrude","CAP_FACE",FACE,{"disambiguationData":[OSD([sQuery(id+"F2.wireOp",EDGE,"E14.14"),sQuery(id+"F2.wireOp",EDGE,"E14.16"),sQuery(id+"F2.wireOp",EDGE,"E14.18"),sQuery(id+"F2.wireOp",EDGE,"E20"),sQuery(id+"F2.wireOp",EDGE,"E21"),sQuery(id+"F2.wireOp",EDGE,"E22.trimOffspring"),sQuery(id+"F2.wireOp",EDGE,"E23")])],"isStart":false});
            var Q16;
            Q16=makeQuery(id+"F16.opChamfer","BLEND_EDGE",EDGE,{"blendedFrom":[makeQuery(id+"F6.opExtrude","CAP_EDGE",EDGE,{"disambiguationData":[OSD([sQuery(id+"F2.wireOp",EDGE,"E20")])],"isStart":false}),makeQuery(id+"F13.opChamfer","BLEND_FACE",FACE,{"disambiguationData":[OSD([sQuery(id+"F2.wireOp",EDGE,"E22.trimOffspring")])]})],"blendedInto":[makeQuery(id+"F13.opChamfer","BLEND_FACE",FACE,{"disambiguationData":[OSD([sQuery(id+"F2.wireOp",EDGE,"E22.trimOffspring")])]})]});
            var Q17;
            Q17=makeQuery(id+"F13.opChamfer","BLEND_EDGE",EDGE,{"blendedFrom":[makeQuery(id+"F6.opExtrude","CAP_EDGE",EDGE,{"disambiguationData":[OSD([sQuery(id+"F2.wireOp",EDGE,"E22.trimOffspring")])],"isStart":false}),makeQuery(id+"F9.opChamfer","BLEND_FACE",FACE,{"disambiguationData":[OSD([sQuery(id+"F2.wireOp",EDGE,"E23")])]})],"blendedInto":[makeQuery(id+"F9.opChamfer","BLEND_FACE",FACE,{"disambiguationData":[OSD([sQuery(id+"F2.wireOp",EDGE,"E23")])]})]});
            var Q18;
            Q18=makeQuery(id+"F9.opChamfer","BLEND_EDGE",EDGE,{"blendedFrom":[makeQuery(id+"F6.opExtrude","CAP_EDGE",EDGE,{"disambiguationData":[OSD([sQuery(id+"F2.wireOp",EDGE,"E14.14")])],"isStart":false}),makeQuery(id+"F6.opExtrude","CAP_EDGE",EDGE,{"disambiguationData":[OSD([sQuery(id+"F2.wireOp",EDGE,"E23")])],"isStart":false})],"blendedInto":[]});
            var Q19;
            Q19=makeQuery(id+"F15.opChamfer","BLEND_EDGE",EDGE,{"blendedFrom":[makeQuery(id+"F6.opExtrude","CAP_EDGE",EDGE,{"disambiguationData":[OSD([sQuery(id+"F2.wireOp",EDGE,"E14.16")])],"isStart":false}),makeQuery(id+"F8.opChamfer","BLEND_FACE",FACE,{"disambiguationData":[OSD([sQuery(id+"F2.wireOp",EDGE,"E14.18")])]})],"blendedInto":[makeQuery(id+"F8.opChamfer","BLEND_FACE",FACE,{"disambiguationData":[OSD([sQuery(id+"F2.wireOp",EDGE,"E14.18")])]})]});
            var Q20;
            Q20=makeQuery(id+"F15.opChamfer","BLEND_EDGE",EDGE,{"blendedFrom":[makeQuery(id+"F6.opExtrude","CAP_EDGE",EDGE,{"disambiguationData":[OSD([sQuery(id+"F2.wireOp",EDGE,"E14.16")])],"isStart":false}),makeQuery(id+"F9.opChamfer","BLEND_FACE",FACE,{"disambiguationData":[OSD([sQuery(id+"F2.wireOp",EDGE,"E14.14")])]})],"blendedInto":[makeQuery(id+"F9.opChamfer","BLEND_FACE",FACE,{"disambiguationData":[OSD([sQuery(id+"F2.wireOp",EDGE,"E14.14")])]})]});
            var Q21;
            Q21=makeQuery(id+"F12.opChamfer","BLEND_EDGE",EDGE,{"blendedFrom":[makeQuery(id+"F6.opExtrude","CAP_EDGE",EDGE,{"disambiguationData":[OSD([sQuery(id+"F2.wireOp",EDGE,"E14.20")])],"isStart":false}),makeQuery(id+"F9.opChamfer","BLEND_FACE",FACE,{"disambiguationData":[OSD([sQuery(id+"F2.wireOp",EDGE,"E16")])]})],"blendedInto":[makeQuery(id+"F9.opChamfer","BLEND_FACE",FACE,{"disambiguationData":[OSD([sQuery(id+"F2.wireOp",EDGE,"E16")])]})]});
            var Q22;
            Q22=makeQuery(id+"F12.opChamfer","BLEND_EDGE",EDGE,{"blendedFrom":[makeQuery(id+"F6.opExtrude","CAP_EDGE",EDGE,{"disambiguationData":[OSD([sQuery(id+"F2.wireOp",EDGE,"E14.20")])],"isStart":false}),makeQuery(id+"F11.opChamfer","BLEND_FACE",FACE,{"disambiguationData":[OSD([sQuery(id+"F2.wireOp",EDGE,"E14.22")])]})],"blendedInto":[makeQuery(id+"F11.opChamfer","BLEND_FACE",FACE,{"disambiguationData":[OSD([sQuery(id+"F2.wireOp",EDGE,"E14.22")])]})]});
            fillet(context, id + "F21", {"entities" : qUnion([Q0, Q1, Q2, Q3, Q4, Q5, Q6, Q7, Q8, Q9, Q10, Q11, Q12, Q13, Q14, Q15, Q16, Q17, Q18, Q19, Q20, Q21, Q22]), "radius" : .5 * mm, "tangentPropagation" : true, "allowEdgeOverflow" : false});
        }
        {
            var Q0;
            Q0=makeQuery(id+"F7.opExtrude","SWEPT_BODY",BODY,{"disambiguationData":[OSD([sQuery(id+"F2.wireOp",EDGE,"E14.2"),sQuery(id+"F2.wireOp",EDGE,"E14.4"),sQuery(id+"F2.wireOp",EDGE,"E14.7"),sQuery(id+"F2.wireOp",EDGE,"E14.9")])]});
            var Q1;
            Q1=makeQuery(id+"F5.opExtrude","SWEPT_BODY",BODY,{"disambiguationData":[OSD([sQuery(id+"F3.wireOp",EDGE,"GxuDiXNE-g7UW-xDb8-DmxE-Lps4FQIEsHQo.bottom"),sQuery(id+"F3.wireOp",EDGE,"GxuDiXNE-g7UW-xDb8-DmxE-Lps4FQIEsHQo.top"),sQuery(id+"F3.wireOp",EDGE,"GxuDiXNE-g7UW-xDb8-DmxE-Lps4FQIEsHQo.left"),sQuery(id+"F3.wireOp",EDGE,"GxuDiXNE-g7UW-xDb8-DmxE-Lps4FQIEsHQo.right")])]});
            var Q2;
            Q2=makeQuery(id+"F1.opExtrude","SWEPT_BODY",BODY,{"disambiguationData":[OSD([sQuery(id+"F0.wireOp",EDGE,"E0"),sQuery(id+"F0.wireOp",EDGE,"E1"),sQuery(id+"F0.wireOp",EDGE,"E2"),sQuery(id+"F0.wireOp",EDGE,"E3"),sQuery(id+"F0.wireOp",EDGE,"E4"),sQuery(id+"F0.wireOp",EDGE,"E5"),sQuery(id+"F0.wireOp",EDGE,"E6"),sQuery(id+"F0.wireOp",EDGE,"E7"),sQuery(id+"F0.wireOp",EDGE,"E8"),sQuery(id+"F0.wireOp",EDGE,"E9"),sQuery(id+"F0.wireOp",EDGE,"E10"),sQuery(id+"F0.wireOp",EDGE,"E13")])]});
            var Q3;
            Q3=makeQuery(id+"F6.opExtrude","SWEPT_BODY",BODY,{"disambiguationData":[OSD([sQuery(id+"F2.wireOp",EDGE,"E14.14"),sQuery(id+"F2.wireOp",EDGE,"E14.16"),sQuery(id+"F2.wireOp",EDGE,"E14.18"),sQuery(id+"F2.wireOp",EDGE,"E20"),sQuery(id+"F2.wireOp",EDGE,"E21"),sQuery(id+"F2.wireOp",EDGE,"E22.trimOffspring"),sQuery(id+"F2.wireOp",EDGE,"E23")])]});
            var Q4;
            Q4=makeQuery(id+"F6.opExtrude","SWEPT_BODY",BODY,{"disambiguationData":[OSD([sQuery(id+"F2.wireOp",EDGE,"E14.0"),sQuery(id+"F2.wireOp",EDGE,"E14.2"),sQuery(id+"F2.wireOp",EDGE,"E14.20"),sQuery(id+"F2.wireOp",EDGE,"E14.22"),sQuery(id+"F2.wireOp",EDGE,"E15"),sQuery(id+"F2.wireOp",EDGE,"E16"),sQuery(id+"F2.wireOp",EDGE,"E17"),sQuery(id+"F2.wireOp",EDGE,"E18"),sQuery(id+"F2.wireOp",EDGE,"E19")])]});
            var Q5;
            Q5=qCreatedBy(makeId("Origin.pointOp"),VERTEX);
            transform(context, id + "F22", {"entities" : qUnion([Q0, Q1, Q2, Q3, Q4]), "transformType" : TransformType.SCALE_UNIFORMLY, "scale" : 2, "scalePoint" : qUnion([Q5]), "makeCopy" : false});
        }
        {
            var Q0;
            Q0=qCreatedBy(makeId("Front.planeOp"),FACE);
            var sketch = newSketch(context, id + "F23", { "sketchPlane" : qUnion([Q0])});
            skCircle(sketch, "E25", {"center": v(0, -18) * mm, "radius": 20 * mm, "construction": true});
            skCircle(sketch, "E26", {"center": v(-60, -18) * mm, "radius": 20 * mm, "construction": true});
            skCircle(sketch, "E27", {"center": v(60, -18) * mm, "radius": 20 * mm, "construction": true});
            skLineSegment(sketch, "E28", {"start": v(77.31, 1.95) * mm, "end": v(77.31, 0) * mm});
            skLineSegment(sketch, "E29", {"start": v(-77.85, 0) * mm, "end": v(-77.85, 1.95) * mm});
            skSolve(sketch);
        }
        {
            var Q0;
            Q0=makeQuery(id+"F1.opExtrude","CAP_FACE",FACE,{"disambiguationData":[OSD([sQuery(id+"F0.wireOp",EDGE,"E0"),sQuery(id+"F0.wireOp",EDGE,"E1"),sQuery(id+"F0.wireOp",EDGE,"E2"),sQuery(id+"F0.wireOp",EDGE,"E3"),sQuery(id+"F0.wireOp",EDGE,"E4"),sQuery(id+"F0.wireOp",EDGE,"E5"),sQuery(id+"F0.wireOp",EDGE,"E6"),sQuery(id+"F0.wireOp",EDGE,"E7"),sQuery(id+"F0.wireOp",EDGE,"E8"),sQuery(id+"F0.wireOp",EDGE,"E9"),sQuery(id+"F0.wireOp",EDGE,"E10"),sQuery(id+"F0.wireOp",EDGE,"E13")])],"isStart":true});
            var Q1;
            Q1=sQuery(id+"F23.wireOp",VERTEX,"E25.center");
            cPlane(context, id + "F24", {"entities" : qUnion([Q0, Q1]), "cplaneType" : CPlaneType.PLANE_POINT, "offset" : 25 * mm, "width" : 150 * mm, "height" : 150 * mm});
        }
        {
            var Q0;
            Q0=qCreatedBy(id+"F24.planeOp",FACE);
            var sketch = newSketch(context, id + "F25", { "sketchPlane" : qUnion([Q0])});
            skPoint(sketch, "E30.0", {"position": v(-60, 0) * mm});
            skPoint(sketch, "E31.0", {"position": v(60, 0) * mm});
            skLineSegment(sketch, "E32.0", {"start": v(-80, 0) * mm, "end": v(-40, 0) * mm, "construction": true});
            skLineSegment(sketch, "E33.0", {"start": v(40, 0) * mm, "end": v(80, 0) * mm, "construction": true});
            skLineSegment(sketch, "E34.0", {"start": v(-20, 0) * mm, "end": v(20, 0) * mm, "construction": true});
            skLineSegment(sketch, "E35", {"start": v(-80, 0) * mm, "end": v(-80, -2) * mm, "construction": true});
            skLineSegment(sketch, "E36.bottom", {"start": v(-79, -4) * mm, "end": v(-81, -4) * mm});
            skLineSegment(sketch, "E36.top", {"start": v(-79, 0) * mm, "end": v(-81, 0) * mm});
            skLineSegment(sketch, "E36.left", {"start": v(-79, -4) * mm, "end": v(-79, 0) * mm});
            skLineSegment(sketch, "E36.right", {"start": v(-81, -4) * mm, "end": v(-81, 0) * mm});
            skPoint(sketch, "E36.middle", {"position": v(-80, -2) * mm});
            skLineSegment(sketch, "E37", {"start": v(80, 0) * mm, "end": v(80, -2) * mm});
            skLineSegment(sketch, "E38.bottom", {"start": v(79, -4) * mm, "end": v(81, -4) * mm});
            skLineSegment(sketch, "E38.top", {"start": v(79, 0) * mm, "end": v(81, 0) * mm});
            skLineSegment(sketch, "E38.left", {"start": v(79, -4) * mm, "end": v(79, 0) * mm});
            skLineSegment(sketch, "E38.right", {"start": v(81, -4) * mm, "end": v(81, 0) * mm});
            skPoint(sketch, "E38.middle", {"position": v(80, -2) * mm});
            skLineSegment(sketch, "E39", {"start": v(-60, 0) * mm, "end": v(-60, 5.87) * mm, "construction": true});
            skLineSegment(sketch, "E40", {"start": v(0, 0) * mm, "end": v(0, 5.64) * mm, "construction": true});
            skLineSegment(sketch, "E41", {"start": v(60, 0) * mm, "end": v(60, 5.37) * mm, "construction": true});
            skLineSegment(sketch, "E42", {"start": v(-20, 0) * mm, "end": v(-20, -2) * mm, "construction": true});
            skLineSegment(sketch, "E43.bottom", {"start": v(-19, -4) * mm, "end": v(-21, -4) * mm});
            skLineSegment(sketch, "E43.top", {"start": v(-19, 0) * mm, "end": v(-21, 0) * mm});
            skLineSegment(sketch, "E43.left", {"start": v(-19, -4) * mm, "end": v(-19, 0) * mm});
            skLineSegment(sketch, "E43.right", {"start": v(-21, -4) * mm, "end": v(-21, 0) * mm});
            skPoint(sketch, "E43.middle", {"position": v(-20, -2) * mm});
            skSolve(sketch);
        }
        {
            var Q0;
            Q0=makeQuery(id+"F25.imprint","IMPRINT",FACE,{"disambiguationData":[TD([[makeQuery(id+"F25.imprint","IMPRINT",EDGE,{"derivedFrom":sQuery(id+"F25.wireOp",EDGE,"E43.bottom")}),-1.0]])]});
            var Q1;
            Q1=sQuery(id+"F25.wireOp",EDGE,"E40");
            revolve(context, id + "F26", {"operationType" : NewBodyOperationType.REMOVE, "entities" : qUnion([Q0]), "axis" : qUnion([Q1]), "revolveType" : RevolveType.FULL, "oppositeDirection" : true});
        }
        {
            var Q0;
            Q0=makeQuery(id+"F25.imprint","IMPRINT",FACE,{"disambiguationData":[TD([[makeQuery(id+"F25.imprint","IMPRINT",EDGE,{"derivedFrom":sQuery(id+"F25.wireOp",EDGE,"E36.bottom")}),-1.0]])]});
            var Q1;
            Q1=sQuery(id+"F25.wireOp",EDGE,"E39");
            revolve(context, id + "F27", {"operationType" : NewBodyOperationType.REMOVE, "entities" : qUnion([Q0]), "axis" : qUnion([Q1]), "revolveType" : RevolveType.FULL, "oppositeDirection" : true});
        }
        {
            var Q0;
            Q0=makeQuery(id+"F25.imprint","IMPRINT",FACE,{"disambiguationData":[TD([[makeQuery(id+"F25.imprint","IMPRINT",EDGE,{"derivedFrom":sQuery(id+"F25.wireOp",EDGE,"E38.bottom")}),1.0]])]});
            var Q1;
            Q1=sQuery(id+"F25.wireOp",EDGE,"E41");
            revolve(context, id + "F28", {"operationType" : NewBodyOperationType.REMOVE, "entities" : qUnion([Q0]), "axis" : qUnion([Q1]), "revolveType" : RevolveType.FULL, "oppositeDirection" : true});
        }
    });
